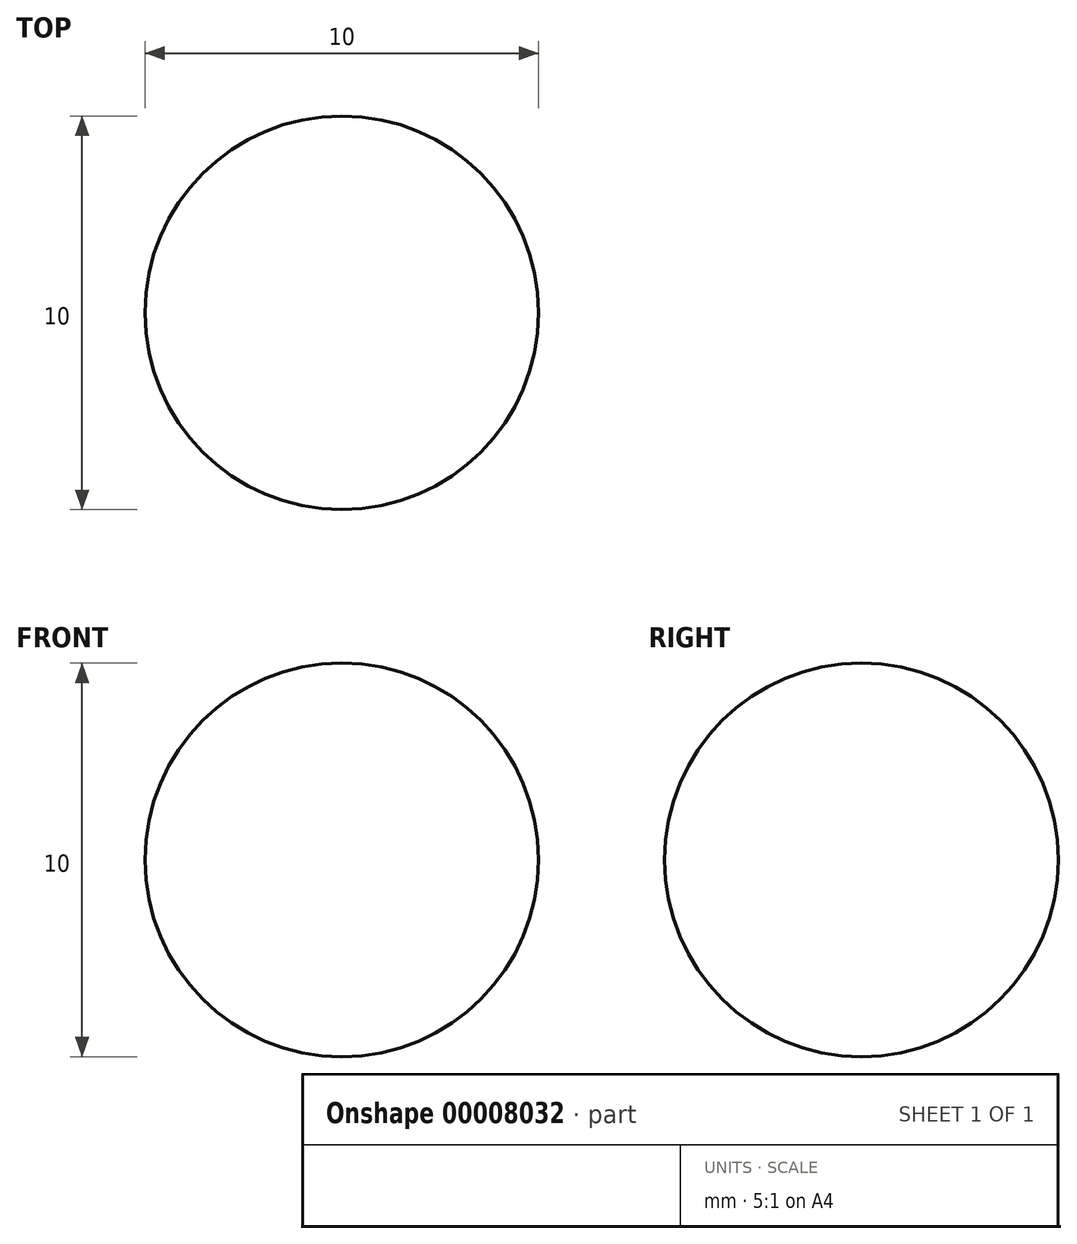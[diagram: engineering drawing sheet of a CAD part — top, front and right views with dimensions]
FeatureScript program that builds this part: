
annotation { "Feature Type Name" : "Feature", "Feature Type Description" : "" }
export const myFeature = defineFeature(function(context is Context, id is Id, definition is map)
    precondition{}
    {
        {
            var Q0;
            Q0=qCreatedBy(makeId("Top.planeOp"),FACE);
            var sketch = newSketch(context, id + "F0", { "sketchPlane" : qUnion([Q0])});
            skArc(sketch, "E0", {"start": v(0, -5) * mm, "mid": v(5, 0) * mm, "end": v(0, 5) * mm});
            skLineSegment(sketch, "E1", {"start": v(0, -261.4) * mm, "end": v(0, 286.77) * mm, "construction": true});
            skLineSegment(sketch, "E2", {"start": v(0, 5) * mm, "end": v(0, -5) * mm});
            skSolve(sketch);
        }
        {
            var Q0;
            Q0=makeQuery(id+"F0.imprint","IMPRINT",FACE,{"disambiguationData":[TD([[makeQuery(id+"F0.imprint","IMPRINT",EDGE,{"derivedFrom":sQuery(id+"F0.wireOp",EDGE,"E0")}),1.0]])]});
            var Q1;
            Q1=sQuery(id+"F0.wireOp",EDGE,"E1");
            revolve(context, id + "F1", {"entities" : qUnion([Q0]), "axis" : qUnion([Q1]), "revolveType" : RevolveType.FULL});
        }
    });
